# Revit family: Seating_Inc-Guest_Mesh
name_source: partatom
category: Furniture
revit_build: Autodesk Revit 2014 (Build: 20130308_1515(x64)
units: mm (PartAtom-declared; Revit-internal decimal feet)

## types (2) — shared parameters
Arm Finish = STI - Plastic Black
Assembly Code = E2020200
Back Finish = STI - Plastic Black
Front Finish = STI - Fabric Black
Glide Finish = STI - Plastic Black
Height = 31 1/2"
Keynote = 12500
Leg Finish = STI - Power Coat - Black
Low Emitting Finish = Yes
Low Emitting Material = Yes
Manufacturer = Seating Inc
Plastic Finish = STI - Plastic Black
Salvage or Reuse = Yes
Seat Finish = STI - Leather
Type Comments = Quick Configuration
URL = www.seatinginc.com
zero-valued in all types: Percentage of Recycled Content

## per-type parameters (varying)
| type | Arm V | Depth | Description | Width |
| Q-3EM43-A | No | 24 1/2" | EDU2 Guest Guest Armless 20.5W x 24.5D x 32H | 20 1/2" |
| Q-3EM44-B | Yes | 23 1/4" | EDU2 Guest Guest with Arms  24.5W x 24.75D x 31.5H | 24" |

note: column(s) folded — value = type name in every type: Model

## geometry (parser evidence)
native form markers: Sweep x4
no freeform markers — native parametric forms only
